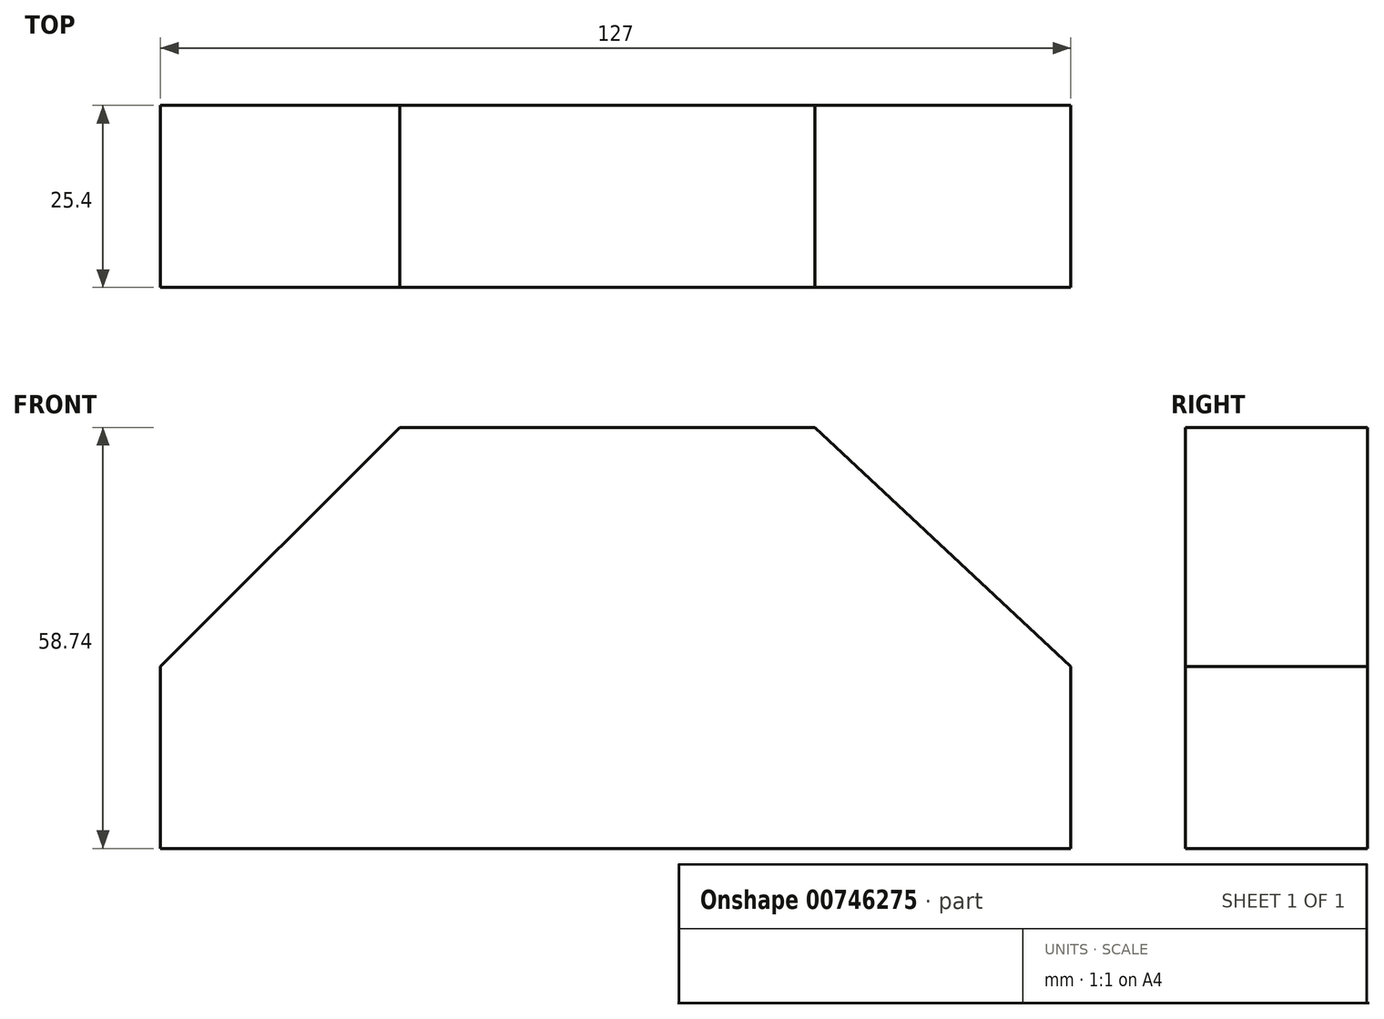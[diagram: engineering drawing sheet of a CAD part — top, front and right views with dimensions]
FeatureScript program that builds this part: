
annotation { "Feature Type Name" : "Feature", "Feature Type Description" : "" }
export const myFeature = defineFeature(function(context is Context, id is Id, definition is map)
    precondition{}
    {
        {
            var Q0;
            Q0=qCreatedBy(makeId("Front.planeOp"),FACE);
            var sketch = newSketch(context, id + "F0", { "sketchPlane" : qUnion([Q0])});
            skLineSegment(sketch, "E0", {"start": v(-64.82, -58.74) * mm, "end": v(62.18, -58.74) * mm});
            skLineSegment(sketch, "E1", {"start": v(62.18, -58.74) * mm, "end": v(62.18, -33.34) * mm});
            skLineSegment(sketch, "E2", {"start": v(62.18, -33.34) * mm, "end": v(26.48, 0) * mm});
            skLineSegment(sketch, "E3", {"start": v(26.48, 0) * mm, "end": v(-31.46, 0) * mm});
            skLineSegment(sketch, "E4", {"start": v(-31.46, 0) * mm, "end": v(-64.82, -33.34) * mm});
            skLineSegment(sketch, "E5", {"start": v(-64.82, -33.34) * mm, "end": v(-64.82, -58.74) * mm});
            skSolve(sketch);
        }
        {
            var Q0;
            Q0=makeQuery(id+"F0.imprint","IMPRINT",FACE,{"disambiguationData":[TD([[makeQuery(id+"F0.imprint","IMPRINT",EDGE,{"derivedFrom":sQuery(id+"F0.wireOp",EDGE,"E0")}),1.0]])]});
            extrude(context, id + "F1", {"entities" : qUnion([Q0]), "depth" : 25.4 * mm, "offsetDistance" : 25.4 * mm});
        }
    });
